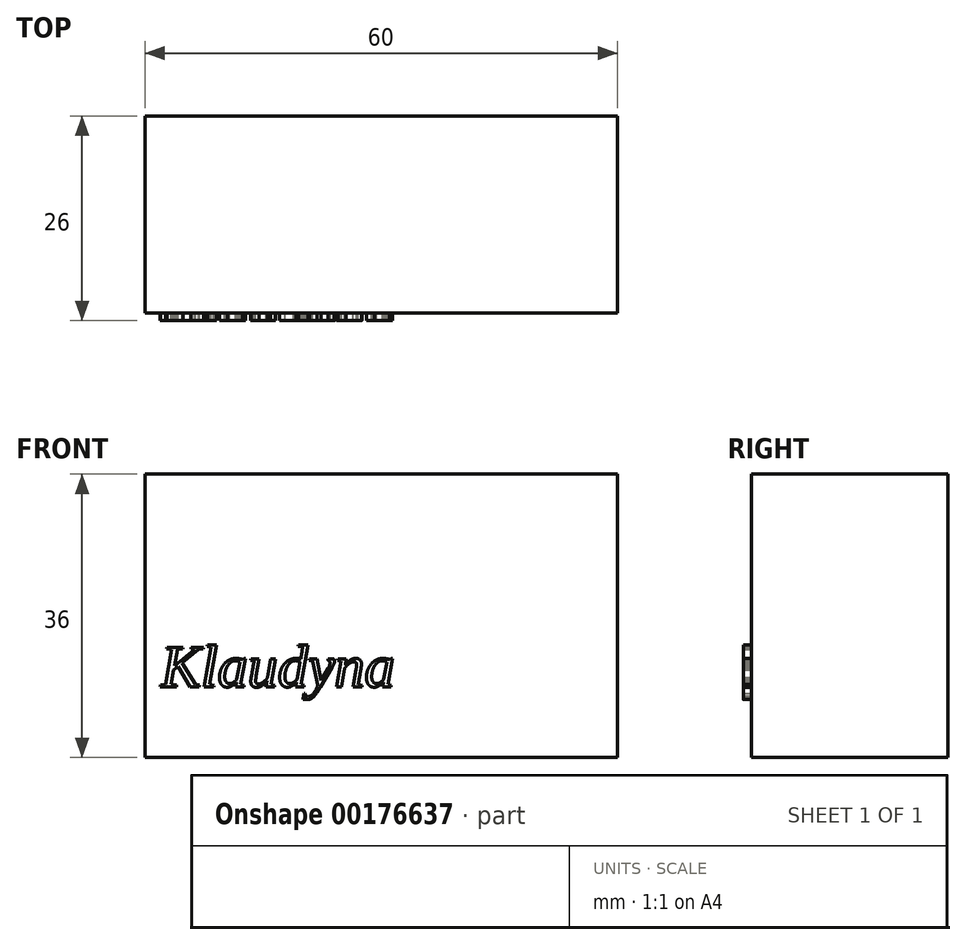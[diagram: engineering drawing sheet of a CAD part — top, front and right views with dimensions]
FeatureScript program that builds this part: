
annotation { "Feature Type Name" : "Feature", "Feature Type Description" : "" }
export const myFeature = defineFeature(function(context is Context, id is Id, definition is map)
    precondition{}
    {
        {
            var Q0;
            Q0=qCreatedBy(makeId("Front.planeOp"),FACE);
            var sketch = newSketch(context, id + "F0", { "sketchPlane" : qUnion([Q0])});
            skLineSegment(sketch, "E0.bottom", {"start": v(0, 0) * mm, "end": v(60, 0) * mm});
            skLineSegment(sketch, "E0.top", {"start": v(0, 36) * mm, "end": v(60, 36) * mm});
            skLineSegment(sketch, "E0.left", {"start": v(0, 0) * mm, "end": v(0, 36) * mm});
            skLineSegment(sketch, "E0.right", {"start": v(60, 0) * mm, "end": v(60, 36) * mm});
            skSolve(sketch);
        }
        {
            var Q0;
            Q0=makeQuery(id+"F0.imprint","IMPRINT",FACE,{"disambiguationData":[TD([[makeQuery(id+"F0.imprint","IMPRINT",EDGE,{"derivedFrom":sQuery(id+"F0.wireOp",EDGE,"E0.bottom")}),1.0]])]});
            extrude(context, id + "F1", {"entities" : qUnion([Q0]), "depth" : 25 * mm});
        }
        {
            var Q0;
            Q0=makeQuery(id+"F1.opExtrude","CAP_FACE",FACE,{"disambiguationData":[OSD([sQuery(id+"F0.wireOp",EDGE,"E0.bottom"),sQuery(id+"F0.wireOp",EDGE,"E0.top"),sQuery(id+"F0.wireOp",EDGE,"E0.left"),sQuery(id+"F0.wireOp",EDGE,"E0.right")])],"isStart":false});
            var sketch = newSketch(context, id + "F2", { "sketchPlane" : qUnion([Q0])});
            skText(sketch, "E1", { "text": "Klaudyna", "fontName": "Tinos-Italic.ttf"});
            const initialGuessF2  = {"E1": [0.002, 0.009, 1, 0, 0.0055]};
            skSetInitialGuess(sketch, initialGuessF2);
            skSolve(sketch);
        }
        {
            var Q0;
            Q0 = qSketchRegion(id + "F2", true);
            extrude(context, id + "F3", {"entities" : qUnion([Q0]), "operationType" : NewBodyOperationType.ADD, "depth" : 1 * mm});
        }
    });
